# Revit family: OK-Celite_Tanque 20 Litros Pequeno_51263
name_source: partatom
category: Plumbing Fixtures
revit_build: Autodesk Revit MEP 2014 (Build: 20131024_2115(x64)
units: mm (PartAtom-declared; Revit-internal decimal feet)

## types (1)
- Branco - 51263
    Assembly Code = D2010400
    CWFU = 0
    Celite: Categoria = Tanques
    Celite: Cores Disponíveis = Branco
    Celite: Código = 51263
    Celite: Descrição = Tanque pequeno para capacidade de 20 litros, cor branca (51263), com mesa para metais, linha Tanques - Louças Celite
    Celite: Desenho Técnico = http://www.celite.com.br
    Celite: Fabricante = Celite
    Celite: Linha = Tanques
    Celite: Link do Produto = http://www.celite.com.br
    Celite: Norma = ABNT NBR 15097-1: 2011 - Requisitos e métodos de ensaio
    Celite: Produto = Louças
    Celite: Tipo = Tanques
    Celite: Versão = Autodesk Revit MEP 2014
    Default Elevation = 0 mm  [stored 0 ft]
    Description = Tanque pequeno para capacidade de 20 litros, cor branca (51263), com mesa para metais, linha Tanques - Louças Celite
    Desenvolvido por = ofcdesk
    Diâmetro Ponto de Esgoto = 40 mm
    HWFU = 0
    Manufacturer = Celite
    Model = 51263
    Raio Ponto de Esgoto = 20 mm
    Selo de Qualidade ofcdesk = Standard
    URL = http://www.celite.com.br
    WFU = 2

note: [stored X ft] marks values corroborated as IEEE doubles in the binary element streams (Revit-internal decimal feet)

## geometry (parser evidence)
native form markers: Blend x4, Sweep x7
no freeform markers — native parametric forms only
